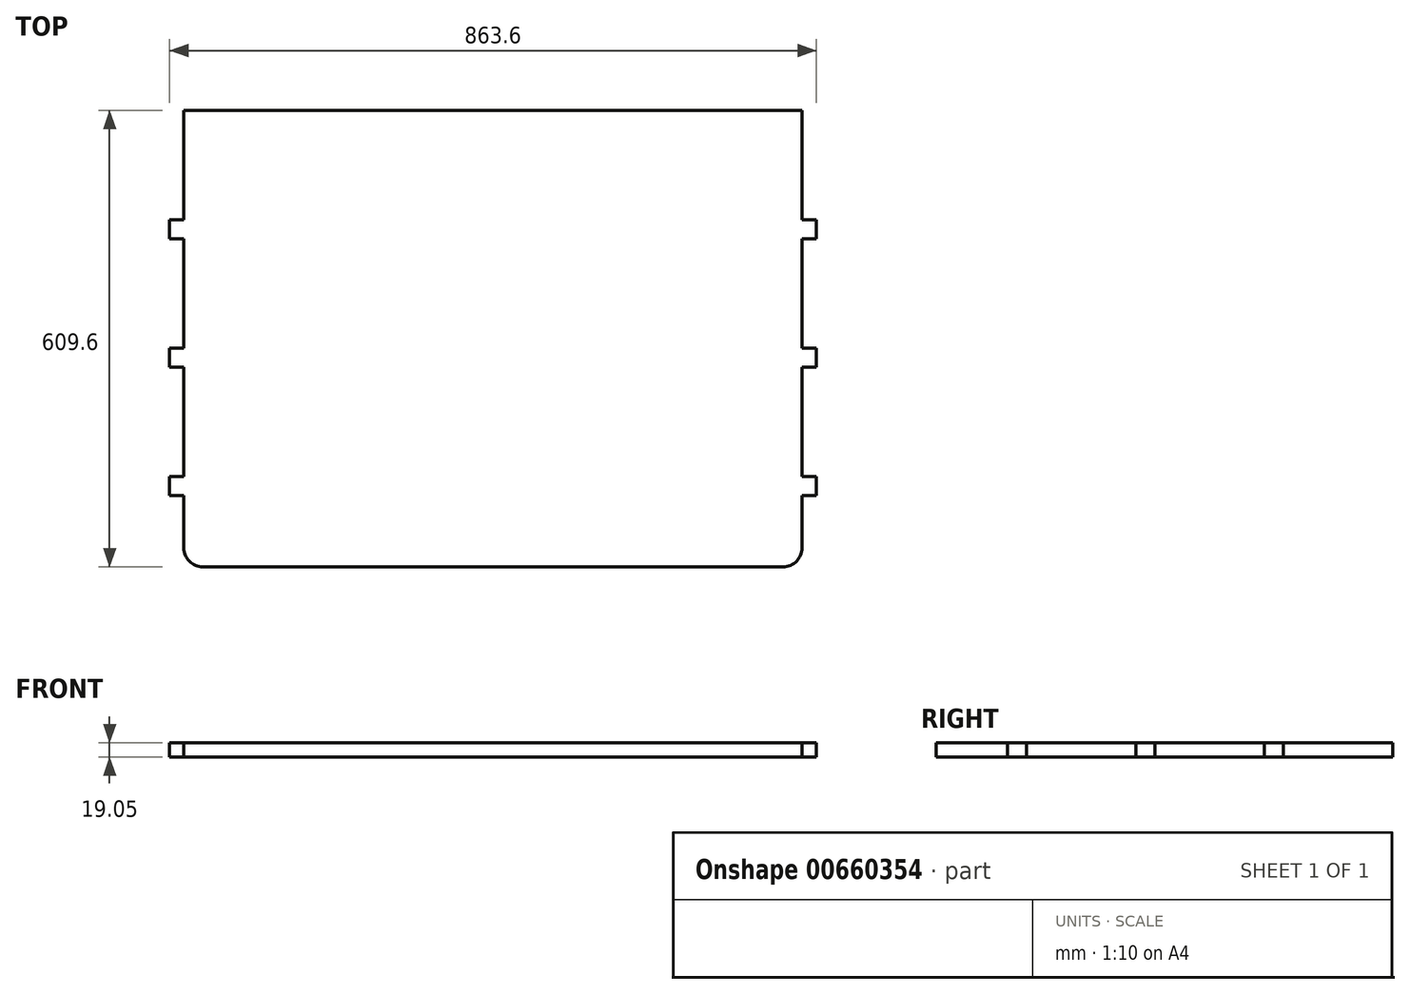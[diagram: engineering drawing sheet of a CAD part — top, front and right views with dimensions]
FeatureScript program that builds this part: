
annotation { "Feature Type Name" : "Feature", "Feature Type Description" : "" }
export const myFeature = defineFeature(function(context is Context, id is Id, definition is map)
    precondition{}
    {
        {
            var Q0;
            Q0=qCreatedBy(makeId("Top.planeOp"),FACE);
            var sketch = newSketch(context, id + "F0", { "sketchPlane" : qUnion([Q0])});
            skLineSegment(sketch, "E0.bottom", {"start": v(-411.6, 342.9) * mm, "end": v(413.9, 342.9) * mm});
            skLineSegment(sketch, "E0.top", {"start": v(-386.2, -266.7) * mm, "end": v(388.5, -266.7) * mm});
            skLineSegment(sketch, "E0.left", {"start": v(-411.6, 342.9) * mm, "end": v(-411.6, -241.3) * mm});
            skLineSegment(sketch, "E0.right", {"start": v(413.9, 342.9) * mm, "end": v(413.9, -241.3) * mm});
            skLineSegment(sketch, "E1.bottom", {"start": v(-411.6, 196.85) * mm, "end": v(-430.65, 196.85) * mm});
            skLineSegment(sketch, "E1.top", {"start": v(-411.6, 171.45) * mm, "end": v(-430.65, 171.45) * mm});
            skLineSegment(sketch, "E1.left", {"start": v(-411.6, 196.85) * mm, "end": v(-411.6, 171.45) * mm});
            skLineSegment(sketch, "E1.right", {"start": v(-430.65, 196.85) * mm, "end": v(-430.65, 171.45) * mm});
            skLineSegment(sketch, "E2.bottom", {"start": v(-411.6, 25.4) * mm, "end": v(-430.65, 25.4) * mm});
            skLineSegment(sketch, "E2.top", {"start": v(-411.6, 0) * mm, "end": v(-430.65, 0) * mm});
            skLineSegment(sketch, "E2.left", {"start": v(-411.6, 25.4) * mm, "end": v(-411.6, 0) * mm});
            skLineSegment(sketch, "E2.right", {"start": v(-430.65, 25.4) * mm, "end": v(-430.65, 0) * mm});
            skLineSegment(sketch, "E3.bottom", {"start": v(413.9, 196.85) * mm, "end": v(432.95, 196.85) * mm});
            skLineSegment(sketch, "E3.top", {"start": v(413.9, 171.45) * mm, "end": v(432.95, 171.45) * mm});
            skLineSegment(sketch, "E3.left", {"start": v(413.9, 196.85) * mm, "end": v(413.9, 171.45) * mm});
            skLineSegment(sketch, "E3.right", {"start": v(432.95, 196.85) * mm, "end": v(432.95, 171.45) * mm});
            skLineSegment(sketch, "E4.bottom", {"start": v(413.9, 25.4) * mm, "end": v(432.95, 25.4) * mm});
            skLineSegment(sketch, "E4.top", {"start": v(413.9, 0) * mm, "end": v(432.95, 0) * mm});
            skLineSegment(sketch, "E4.left", {"start": v(413.9, 25.4) * mm, "end": v(413.9, 0) * mm});
            skLineSegment(sketch, "E4.right", {"start": v(432.95, 25.4) * mm, "end": v(432.95, 0) * mm});
            skLineSegment(sketch, "E5.bottom", {"start": v(-411.6, -146.05) * mm, "end": v(-430.65, -146.05) * mm});
            skLineSegment(sketch, "E5.top", {"start": v(-411.6, -171.45) * mm, "end": v(-430.65, -171.45) * mm});
            skLineSegment(sketch, "E5.left", {"start": v(-411.6, -146.05) * mm, "end": v(-411.6, -171.45) * mm});
            skLineSegment(sketch, "E5.right", {"start": v(-430.65, -146.05) * mm, "end": v(-430.65, -171.45) * mm});
            skLineSegment(sketch, "E6.bottom", {"start": v(413.9, -146.05) * mm, "end": v(432.95, -146.05) * mm});
            skLineSegment(sketch, "E6.top", {"start": v(413.9, -171.45) * mm, "end": v(432.95, -171.45) * mm});
            skLineSegment(sketch, "E6.left", {"start": v(413.9, -146.05) * mm, "end": v(413.9, -171.45) * mm});
            skLineSegment(sketch, "E6.right", {"start": v(432.95, -146.05) * mm, "end": v(432.95, -171.45) * mm});
            skPoint(sketch, "E7.visualSharp", {"position": v(-411.6, -266.7) * mm});
            skArc(sketch, "E7.filletArc", {"start": v(-411.6, -241.3) * mm, "mid": v(-404.16, -259.26) * mm, "end": v(-386.2, -266.7) * mm});
            skPoint(sketch, "E8.visualSharp", {"position": v(413.9, -266.7) * mm});
            skArc(sketch, "E8.filletArc", {"start": v(388.5, -266.7) * mm, "mid": v(406.46, -259.26) * mm, "end": v(413.9, -241.3) * mm});
            skSolve(sketch);
        }
        {
            var Q0;
            Q0 = qSketchRegion(id + "F0", true);
            extrude(context, id + "F1", {"entities" : qUnion([Q0]), "depth" : 19.05 * mm, "offsetDistance" : 25.4 * mm});
        }
    });
